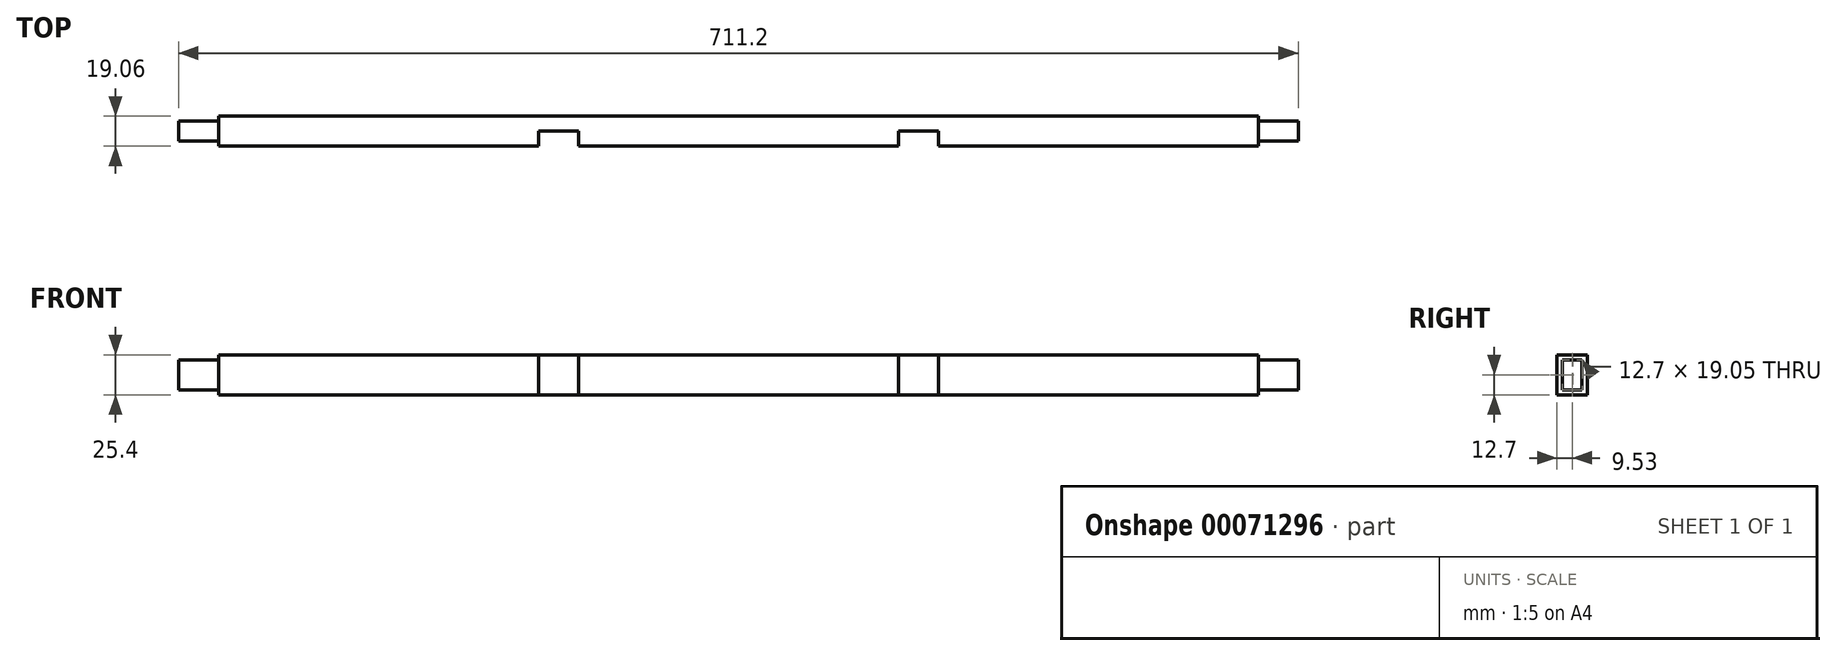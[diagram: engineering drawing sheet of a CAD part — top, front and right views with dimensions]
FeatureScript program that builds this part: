
annotation { "Feature Type Name" : "Feature", "Feature Type Description" : "" }
export const myFeature = defineFeature(function(context is Context, id is Id, definition is map)
    precondition{}
    {
        {
            var Q0;
            Q0=qCreatedBy(makeId("Front.planeOp"),FACE);
            var sketch = newSketch(context, id + "F0", { "sketchPlane" : qUnion([Q0])});
            skLineSegment(sketch, "E0.bottom", {"start": v(-330.2, 12.7) * mm, "end": v(330.2, 12.7) * mm});
            skLineSegment(sketch, "E0.top", {"start": v(-330.2, -12.7) * mm, "end": v(330.2, -12.7) * mm});
            skLineSegment(sketch, "E0.left", {"start": v(-330.2, 12.7) * mm, "end": v(-330.2, -12.7) * mm});
            skLineSegment(sketch, "E0.right", {"start": v(330.2, 12.7) * mm, "end": v(330.2, -12.7) * mm});
            skSolve(sketch);
        }
        {
            var Q0;
            Q0=makeQuery(id+"F0.imprint","IMPRINT",FACE,{"disambiguationData":[TD([[makeQuery(id+"F0.imprint","IMPRINT",EDGE,{"derivedFrom":sQuery(id+"F0.wireOp",EDGE,"E0.bottom")}),-1.0]])]});
            extrude(context, id + "F1", {"entities" : qUnion([Q0]), "endBound" : BoundingType.SYMMETRIC, "depth" : 19.05 * mm});
        }
        {
            var Q0;
            Q0=makeQuery(id+"F1.opExtrude","CAP_FACE",FACE,{"disambiguationData":[OSD([sQuery(id+"F0.wireOp",EDGE,"E0.bottom"),sQuery(id+"F0.wireOp",EDGE,"E0.top"),sQuery(id+"F0.wireOp",EDGE,"E0.left"),sQuery(id+"F0.wireOp",EDGE,"E0.right")])],"isStart":false});
            var sketch = newSketch(context, id + "F2", { "sketchPlane" : qUnion([Q0])});
            skLineSegment(sketch, "E1.bottom", {"start": v(-127, 12.7) * mm, "end": v(-101.6, 12.7) * mm});
            skLineSegment(sketch, "E1.top", {"start": v(-127, -12.7) * mm, "end": v(-101.6, -12.7) * mm});
            skLineSegment(sketch, "E1.left", {"start": v(-127, 12.7) * mm, "end": v(-127, -12.7) * mm});
            skLineSegment(sketch, "E1.right", {"start": v(-101.6, 12.7) * mm, "end": v(-101.6, -12.7) * mm});
            skLineSegment(sketch, "E2.bottom", {"start": v(101.6, 12.7) * mm, "end": v(127, 12.7) * mm});
            skLineSegment(sketch, "E2.top", {"start": v(101.6, -12.7) * mm, "end": v(127, -12.7) * mm});
            skLineSegment(sketch, "E2.left", {"start": v(101.6, 12.7) * mm, "end": v(101.6, -12.7) * mm});
            skLineSegment(sketch, "E2.right", {"start": v(127, 12.7) * mm, "end": v(127, -12.7) * mm});
            skSolve(sketch);
        }
        {
            var Q0;
            Q0=makeQuery(id+"F2.imprint","IMPRINT",FACE,{"disambiguationData":[TD([[makeQuery(id+"F2.imprint","IMPRINT",EDGE,{"derivedFrom":sQuery(id+"F2.wireOp",EDGE,"E1.bottom")}),-1.0]])]});
            extrude(context, id + "F3", {"entities" : qUnion([Q0]), "operationType" : NewBodyOperationType.REMOVE, "oppositeDirection" : true, "depth" : 9.52 * mm});
        }
        {
            var Q0;
            Q0=makeQuery(id+"F2.imprint","IMPRINT",FACE,{"disambiguationData":[TD([[makeQuery(id+"F2.imprint","IMPRINT",EDGE,{"derivedFrom":sQuery(id+"F2.wireOp",EDGE,"E2.bottom")}),-1.0]])]});
            extrude(context, id + "F4", {"entities" : qUnion([Q0]), "operationType" : NewBodyOperationType.REMOVE, "oppositeDirection" : true, "depth" : 9.52 * mm});
        }
        {
            var Q0;
            Q0=makeQuery(id+"F1.opExtrude","SWEPT_FACE",FACE,{"disambiguationData":[OSD([sQuery(id+"F0.wireOp",EDGE,"E0.right")])]});
            var sketch = newSketch(context, id + "F5", { "sketchPlane" : qUnion([Q0])});
            skLineSegment(sketch, "E3.bottom", {"start": v(-6.35, 9.52) * mm, "end": v(6.35, 9.52) * mm});
            skLineSegment(sketch, "E3.top", {"start": v(-6.35, -9.53) * mm, "end": v(6.35, -9.53) * mm});
            skLineSegment(sketch, "E3.left", {"start": v(-6.35, 9.52) * mm, "end": v(-6.35, -9.53) * mm});
            skLineSegment(sketch, "E3.right", {"start": v(6.35, 9.52) * mm, "end": v(6.35, -9.53) * mm});
            skSolve(sketch);
        }
        {
            var Q0;
            Q0=makeQuery(id+"F1.opExtrude","SWEPT_FACE",FACE,{"disambiguationData":[OSD([sQuery(id+"F0.wireOp",EDGE,"E0.left")])]});
            var sketch = newSketch(context, id + "F6", { "sketchPlane" : qUnion([Q0])});
            skLineSegment(sketch, "E4.bottom", {"start": v(-6.35, 9.53) * mm, "end": v(6.35, 9.53) * mm});
            skLineSegment(sketch, "E4.top", {"start": v(-6.35, -9.53) * mm, "end": v(6.35, -9.53) * mm});
            skLineSegment(sketch, "E4.left", {"start": v(-6.35, 9.53) * mm, "end": v(-6.35, -9.53) * mm});
            skLineSegment(sketch, "E4.right", {"start": v(6.35, 9.53) * mm, "end": v(6.35, -9.53) * mm});
            skSolve(sketch);
        }
        {
            var Q0;
            Q0=makeQuery(id+"F5.imprint","IMPRINT",FACE,{"disambiguationData":[TD([[makeQuery(id+"F5.imprint","IMPRINT",EDGE,{"derivedFrom":sQuery(id+"F5.wireOp",EDGE,"E3.bottom")}),-1.0]])]});
            extrude(context, id + "F7", {"entities" : qUnion([Q0]), "operationType" : NewBodyOperationType.ADD, "depth" : 25.4 * mm});
        }
        {
            var Q0;
            Q0=makeQuery(id+"F6.imprint","IMPRINT",FACE,{"disambiguationData":[TD([[makeQuery(id+"F6.imprint","IMPRINT",EDGE,{"derivedFrom":sQuery(id+"F6.wireOp",EDGE,"E4.bottom")}),-1.0]])]});
            extrude(context, id + "F8", {"entities" : qUnion([Q0]), "operationType" : NewBodyOperationType.ADD, "depth" : 25.4 * mm});
        }
    });
